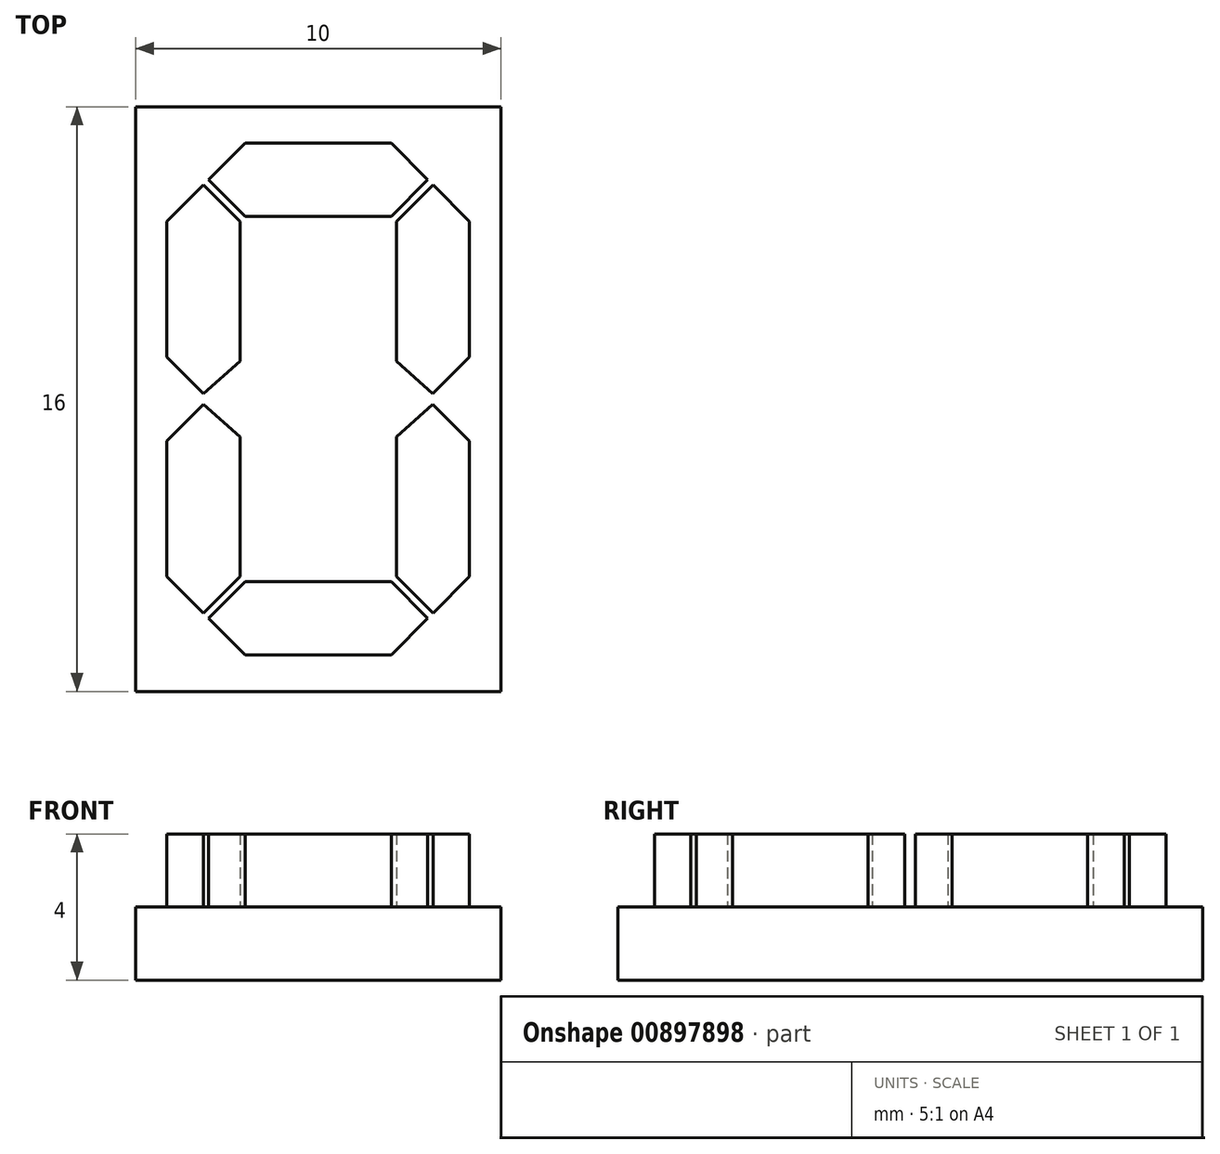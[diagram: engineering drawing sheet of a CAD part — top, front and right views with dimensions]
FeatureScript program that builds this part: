
annotation { "Feature Type Name" : "Feature", "Feature Type Description" : "" }
export const myFeature = defineFeature(function(context is Context, id is Id, definition is map)
    precondition{}
    {
        {
            var Q0;
            Q0=qCreatedBy(makeId("Top.planeOp"),FACE);
            var sketch = newSketch(context, id + "F0", { "sketchPlane" : qUnion([Q0])});
            skLineSegment(sketch, "E0.bottom", {"start": v(5, -8) * mm, "end": v(-5, -8) * mm});
            skLineSegment(sketch, "E0.top", {"start": v(5, 8) * mm, "end": v(-5, 8) * mm});
            skLineSegment(sketch, "E0.left", {"start": v(5, -8) * mm, "end": v(5, 8) * mm});
            skLineSegment(sketch, "E0.right", {"start": v(-5, -8) * mm, "end": v(-5, 8) * mm});
            skPoint(sketch, "E0.middle", {"position": v(0, 0) * mm});
            skSolve(sketch);
        }
        {
            var Q0;
            Q0=makeQuery(id+"F0.imprint","IMPRINT",FACE,{"disambiguationData":[TD([[makeQuery(id+"F0.imprint","IMPRINT",EDGE,{"derivedFrom":sQuery(id+"F0.wireOp",EDGE,"E0.bottom")}),-1.0]])]});
            extrude(context, id + "F1", {"entities" : qUnion([Q0]), "depth" : 2 * mm, "offsetDistance" : 25 * mm});
        }
        {
            var Q0;
            Q0=makeQuery(id+"F1.opExtrude","CAP_FACE",FACE,{"disambiguationData":[OSD([sQuery(id+"F0.wireOp",EDGE,"E0.bottom"),sQuery(id+"F0.wireOp",EDGE,"E0.top"),sQuery(id+"F0.wireOp",EDGE,"E0.left"),sQuery(id+"F0.wireOp",EDGE,"E0.right")])],"isStart":false});
            var sketch = newSketch(context, id + "F2", { "sketchPlane" : qUnion([Q0])});
            skLineSegment(sketch, "E1", {"start": v(-3, 8) * mm, "end": v(-3, -8) * mm, "construction": true});
            skLineSegment(sketch, "E2.0.1.0", {"start": v(-5, 6) * mm, "end": v(5, 6) * mm, "construction": true});
            skLineSegment(sketch, "E2.direction2", {"start": v(-5, 7) * mm, "end": v(-5, 6) * mm, "construction": true});
            skLineSegment(sketch, "E3.1.0.0", {"start": v(-2, 8) * mm, "end": v(-2, -8) * mm, "construction": true});
            skLineSegment(sketch, "E3.3.0.0", {"start": v(0, 8) * mm, "end": v(0, -8) * mm, "construction": true});
            skLineSegment(sketch, "E3.direction1", {"start": v(-3, -8) * mm, "end": v(-2, -8) * mm, "construction": true});
            skLineSegment(sketch, "E4", {"start": v(-2, 7) * mm, "end": v(-3, 6) * mm});
            skLineSegment(sketch, "E5", {"start": v(-3, 6) * mm, "end": v(-2, 5) * mm});
            skLineSegment(sketch, "E6", {"start": v(-2, 5) * mm, "end": v(0, 5) * mm});
            skLineSegment(sketch, "E7", {"start": v(-2, 7) * mm, "end": v(0, 7) * mm});
            skLineSegment(sketch, "E8.0", {"start": v(-3.14, 5.86) * mm, "end": v(-2.14, 4.86) * mm});
            skLineSegment(sketch, "E9", {"start": v(-2.14, 4.86) * mm, "end": v(-2.14, 1.03) * mm});
            skLineSegment(sketch, "E10.0", {"start": v(-4.14, 4.86) * mm, "end": v(-4.14, 1.15) * mm});
            skLineSegment(sketch, "E11", {"start": v(-3.14, 5.86) * mm, "end": v(-4.14, 4.86) * mm});
            skLineSegment(sketch, "E12", {"start": v(-4.14, 4.86) * mm, "end": v(5, 4.86) * mm, "construction": true});
            skLineSegment(sketch, "E13", {"start": v(-2, 0.9) * mm, "end": v(-3, 0) * mm});
            skLineSegment(sketch, "E14.0", {"start": v(-2.14, 1.03) * mm, "end": v(-3.14, 0.15) * mm});
            skLineSegment(sketch, "E15", {"start": v(-3.14, 5.86) * mm, "end": v(-3.14, 0.15) * mm, "construction": true});
            skLineSegment(sketch, "E16", {"start": v(-4.14, 1.15) * mm, "end": v(-3.14, 0.15) * mm});
            skLineSegment(sketch, "E17.MirrorCS", {"start": v(-2, -0.9) * mm, "end": v(-3, 0) * mm});
            skLineSegment(sketch, "E18.MirrorCS", {"start": v(-2, -5) * mm, "end": v(0, -5) * mm});
            skLineSegment(sketch, "E19.MirrorCS", {"start": v(-3, -6) * mm, "end": v(-2, -5) * mm});
            skLineSegment(sketch, "E20.MirrorCS", {"start": v(-2, -7) * mm, "end": v(-3, -6) * mm});
            skLineSegment(sketch, "E21.MirrorCS", {"start": v(-2, -7) * mm, "end": v(0, -7) * mm});
            skLineSegment(sketch, "E22.MirrorCS", {"start": v(-3.14, -5.86) * mm, "end": v(-2.14, -4.86) * mm});
            skLineSegment(sketch, "E23.MirrorCS", {"start": v(-3.14, -5.86) * mm, "end": v(-4.14, -4.86) * mm});
            skLineSegment(sketch, "E24.MirrorCS", {"start": v(-4.14, -4.86) * mm, "end": v(-4.14, -1.15) * mm});
            skLineSegment(sketch, "E25.MirrorCS", {"start": v(-4.14, -1.15) * mm, "end": v(-3.14, -0.15) * mm});
            skLineSegment(sketch, "E26.MirrorCS", {"start": v(-2.14, -4.86) * mm, "end": v(-2.14, -1.03) * mm});
            skLineSegment(sketch, "E27.MirrorCS", {"start": v(-2.14, -1.03) * mm, "end": v(-3.14, -0.15) * mm});
            skLineSegment(sketch, "E28.MirrorCS", {"start": v(2, 7) * mm, "end": v(0, 7) * mm});
            skLineSegment(sketch, "E29.MirrorCS", {"start": v(2, 7) * mm, "end": v(3, 6) * mm});
            skLineSegment(sketch, "E30.MirrorCS", {"start": v(3, 6) * mm, "end": v(2, 5) * mm});
            skLineSegment(sketch, "E31.MirrorCS", {"start": v(2, 5) * mm, "end": v(0, 5) * mm});
            skLineSegment(sketch, "E32.MirrorCS", {"start": v(3.14, 5.86) * mm, "end": v(2.14, 4.86) * mm});
            skLineSegment(sketch, "E33.MirrorCS", {"start": v(3.14, 5.86) * mm, "end": v(4.14, 4.86) * mm});
            skLineSegment(sketch, "E34.MirrorCS", {"start": v(4.14, 4.86) * mm, "end": v(4.14, 1.15) * mm});
            skLineSegment(sketch, "E35.MirrorCS", {"start": v(4.14, 1.15) * mm, "end": v(3.14, 0.15) * mm});
            skLineSegment(sketch, "E36.MirrorCS", {"start": v(2.14, 4.86) * mm, "end": v(2.14, 1.03) * mm});
            skLineSegment(sketch, "E37.MirrorCS", {"start": v(2.14, 1.03) * mm, "end": v(3.14, 0.15) * mm});
            skLineSegment(sketch, "E38.MirrorCS", {"start": v(2, 0.9) * mm, "end": v(3, 0) * mm});
            skLineSegment(sketch, "E39.MirrorCS", {"start": v(2, -0.9) * mm, "end": v(3, 0) * mm});
            skLineSegment(sketch, "E40.MirrorCS", {"start": v(2.14, -1.03) * mm, "end": v(3.14, -0.15) * mm});
            skLineSegment(sketch, "E41.MirrorCS", {"start": v(4.14, -1.15) * mm, "end": v(3.14, -0.15) * mm});
            skLineSegment(sketch, "E42.MirrorCS", {"start": v(4.14, -4.86) * mm, "end": v(4.14, -1.15) * mm});
            skLineSegment(sketch, "E43.MirrorCS", {"start": v(2.14, -4.86) * mm, "end": v(2.14, -1.03) * mm});
            skLineSegment(sketch, "E44.MirrorCS", {"start": v(3.14, -5.86) * mm, "end": v(2.14, -4.86) * mm});
            skLineSegment(sketch, "E45.MirrorCS", {"start": v(3.14, -5.86) * mm, "end": v(4.14, -4.86) * mm});
            skLineSegment(sketch, "E46.MirrorCS", {"start": v(3, -6) * mm, "end": v(2, -5) * mm});
            skLineSegment(sketch, "E47.MirrorCS", {"start": v(2, -5) * mm, "end": v(0, -5) * mm});
            skLineSegment(sketch, "E48.MirrorCS", {"start": v(2, -7) * mm, "end": v(3, -6) * mm});
            skLineSegment(sketch, "E49.MirrorCS", {"start": v(2, -7) * mm, "end": v(0, -7) * mm});
            skSolve(sketch);
        }
        {
            var Q0;
            Q0=qSketchRegion(id+"F2",true);
            extrude(context, id + "F3", {"entities" : qUnion([Q0]), "operationType" : NewBodyOperationType.ADD, "depth" : 2 * mm, "offsetDistance" : 25 * mm});
        }
    });
